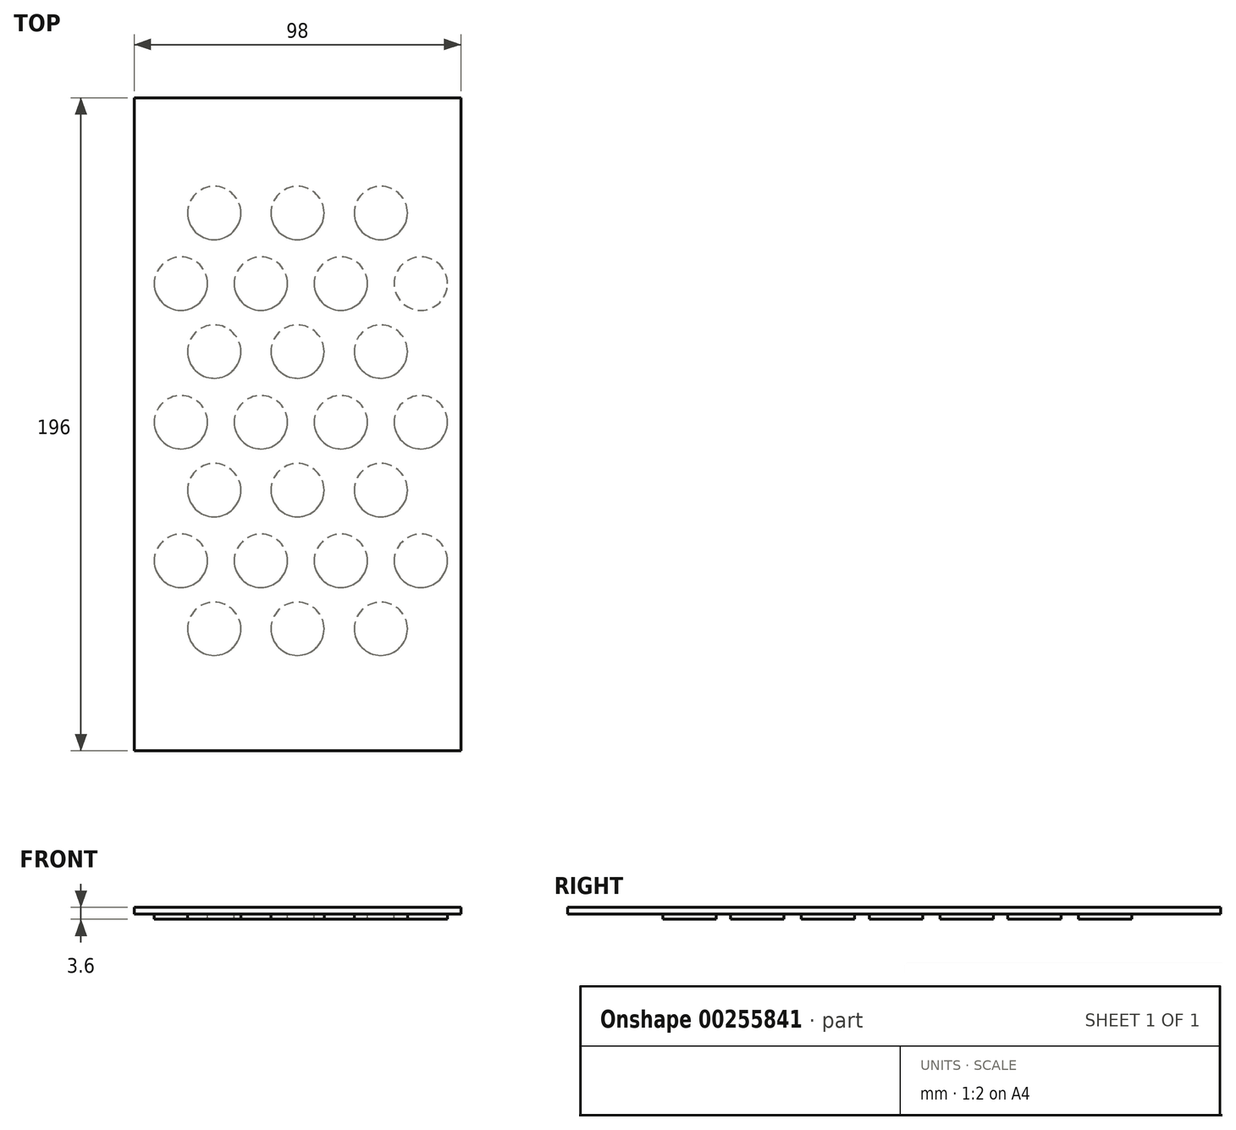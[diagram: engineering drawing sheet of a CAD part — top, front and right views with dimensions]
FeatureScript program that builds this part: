
annotation { "Feature Type Name" : "Feature", "Feature Type Description" : "" }
export const myFeature = defineFeature(function(context is Context, id is Id, definition is map)
    precondition{}
    {
        {
            var Q0;
            Q0=qCreatedBy(makeId("Top.planeOp"),FACE);
            var sketch = newSketch(context, id + "F0", { "sketchPlane" : qUnion([Q0])});
            skLineSegment(sketch, "E0.bottom", {"start": v(49, 98) * mm, "end": v(-49, 98) * mm});
            skLineSegment(sketch, "E0.top", {"start": v(49, -98) * mm, "end": v(-49, -98) * mm});
            skLineSegment(sketch, "E0.left", {"start": v(49, 98) * mm, "end": v(49, -98) * mm});
            skLineSegment(sketch, "E0.right", {"start": v(-49, 98) * mm, "end": v(-49, -98) * mm});
            skPoint(sketch, "E0.middle", {"position": v(0, 0) * mm});
            skSolve(sketch);
        }
        {
            var Q0;
            Q0=makeQuery(id+"F0.imprint","IMPRINT",FACE,{"disambiguationData":[TD([[makeQuery(id+"F0.imprint","IMPRINT",EDGE,{"derivedFrom":sQuery(id+"F0.wireOp",EDGE,"E0.bottom")}),1.0]])]});
            extrude(context, id + "F1", {"entities" : qUnion([Q0]), "depth" : 2 * mm, "offsetDistance" : 25 * mm});
        }
        {
            var Q0;
            Q0=makeQuery(id+"F1.opExtrude","CAP_FACE",FACE,{"disambiguationData":[OSD([sQuery(id+"F0.wireOp",EDGE,"E0.bottom"),sQuery(id+"F0.wireOp",EDGE,"E0.top"),sQuery(id+"F0.wireOp",EDGE,"E0.left"),sQuery(id+"F0.wireOp",EDGE,"E0.right")])],"isStart":true});
            var sketch = newSketch(context, id + "F2", { "sketchPlane" : qUnion([Q0])});
            skCircle(sketch, "E1", {"center": v(37, -42.2) * mm, "radius": 8 * mm});
            skCircle(sketch, "E2.0.1.0", {"center": v(37, -0.6) * mm, "radius": 8 * mm});
            skCircle(sketch, "E2.0.2.0", {"center": v(37, 41) * mm, "radius": 8 * mm});
            skCircle(sketch, "E2.1.0.0", {"center": v(13, -42.2) * mm, "radius": 8 * mm});
            skCircle(sketch, "E2.1.1.0", {"center": v(13, -0.6) * mm, "radius": 8 * mm});
            skCircle(sketch, "E2.1.2.0", {"center": v(13, 41) * mm, "radius": 8 * mm});
            skLineSegment(sketch, "E2.direction1", {"start": v(37, -42.2) * mm, "end": v(13, -42.2) * mm, "construction": true});
            skLineSegment(sketch, "E2.direction2", {"start": v(37, -42.2) * mm, "end": v(37, -0.6) * mm, "construction": true});
            skCircle(sketch, "E3.0.2.0", {"center": v(-11, -42.2) * mm, "radius": 8 * mm});
            skCircle(sketch, "E3.0.2.1", {"center": v(-11, -0.6) * mm, "radius": 8 * mm});
            skCircle(sketch, "E3.0.2.2", {"center": v(-11, 41) * mm, "radius": 8 * mm});
            skCircle(sketch, "E3.0.3.0", {"center": v(-35, -42.2) * mm, "radius": 8 * mm});
            skCircle(sketch, "E3.0.3.1", {"center": v(-35, -0.6) * mm, "radius": 8 * mm});
            skCircle(sketch, "E3.0.3.2", {"center": v(-35, 41) * mm, "radius": 8 * mm});
            skCircle(sketch, "E4", {"center": v(-25, -63.4) * mm, "radius": 8 * mm});
            skCircle(sketch, "E5.0.1.0", {"center": v(-25, -21.8) * mm, "radius": 8 * mm});
            skCircle(sketch, "E5.0.2.0", {"center": v(-25, 19.8) * mm, "radius": 8 * mm});
            skCircle(sketch, "E5.1.0.0", {"center": v(0, -63.4) * mm, "radius": 8 * mm});
            skCircle(sketch, "E5.1.1.0", {"center": v(0, -21.8) * mm, "radius": 8 * mm});
            skCircle(sketch, "E5.1.2.0", {"center": v(0, 19.8) * mm, "radius": 8 * mm});
            skCircle(sketch, "E5.2.0.0", {"center": v(25, -63.4) * mm, "radius": 8 * mm});
            skCircle(sketch, "E5.2.1.0", {"center": v(25, -21.8) * mm, "radius": 8 * mm});
            skCircle(sketch, "E5.2.2.0", {"center": v(25, 19.8) * mm, "radius": 8 * mm});
            skLineSegment(sketch, "E5.direction1", {"start": v(-25, -63.4) * mm, "end": v(0, -63.4) * mm, "construction": true});
            skLineSegment(sketch, "E5.direction2", {"start": v(-25, -63.4) * mm, "end": v(-25, -21.8) * mm, "construction": true});
            skCircle(sketch, "E6.0.0.3", {"center": v(-25, 61.4) * mm, "radius": 8 * mm});
            skCircle(sketch, "E6.0.1.3", {"center": v(0, 61.4) * mm, "radius": 8 * mm});
            skCircle(sketch, "E6.0.2.3", {"center": v(25, 61.4) * mm, "radius": 8 * mm});
            skSolve(sketch);
        }
        {
            var Q0;
            Q0 = qSketchRegion(id + "F2", true);
            extrude(context, id + "F3", {"entities" : qUnion([Q0]), "operationType" : NewBodyOperationType.ADD, "depth" : 1.6 * mm, "offsetDistance" : 25 * mm});
        }
    });
